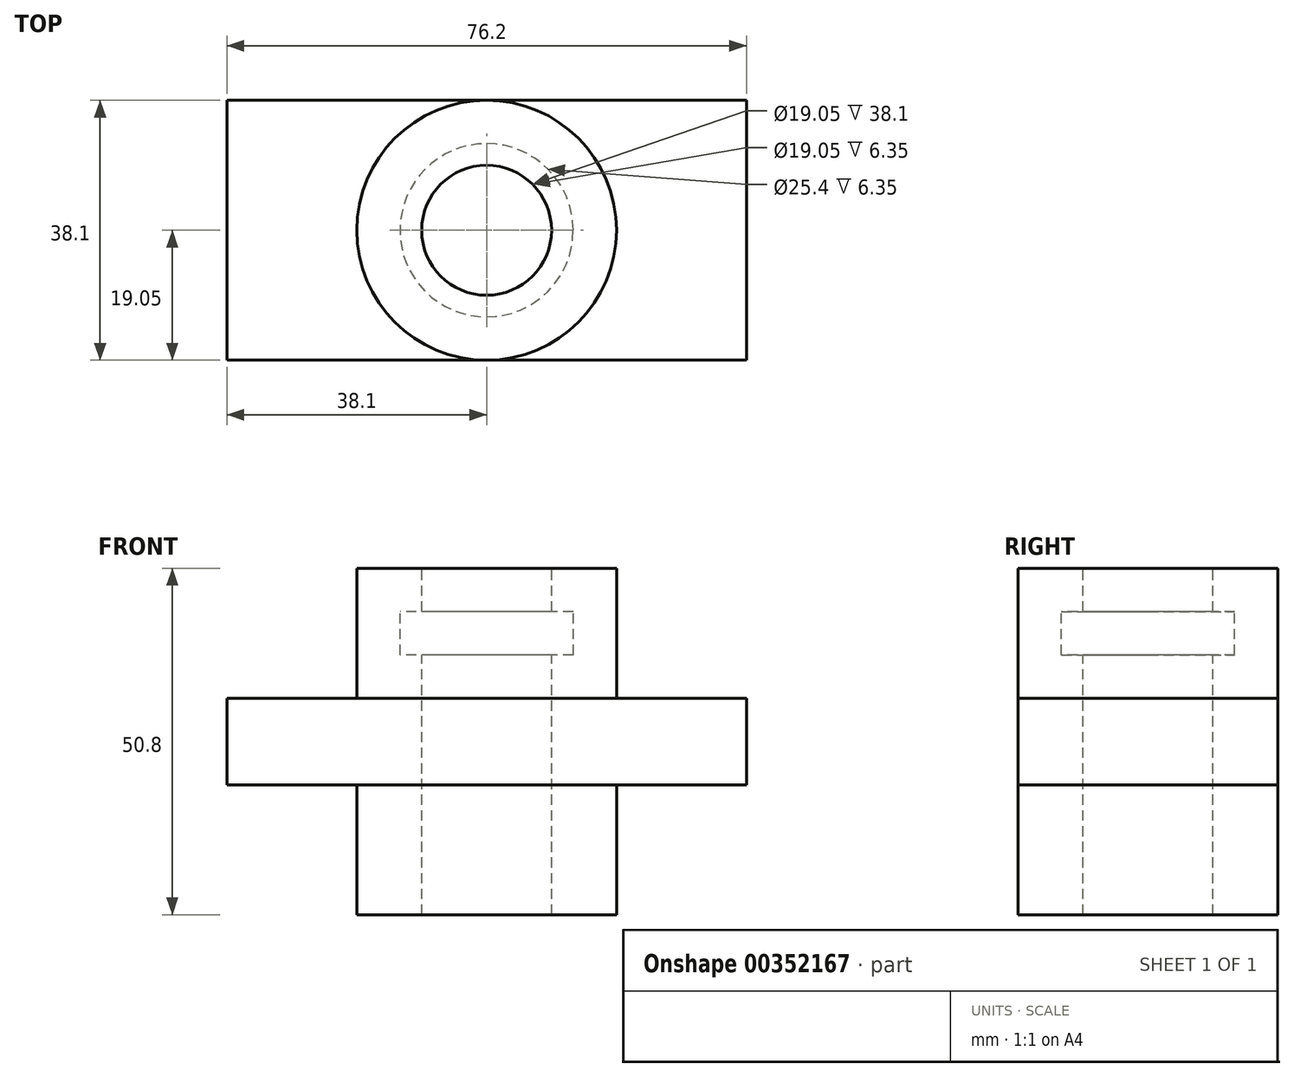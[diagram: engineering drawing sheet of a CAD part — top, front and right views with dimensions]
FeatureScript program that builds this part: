
annotation { "Feature Type Name" : "Feature", "Feature Type Description" : "" }
export const myFeature = defineFeature(function(context is Context, id is Id, definition is map)
    precondition{}
    {
        {
            var Q0;
            Q0=qCreatedBy(makeId("Top.planeOp"),FACE);
            var sketch = newSketch(context, id + "F0", { "sketchPlane" : qUnion([Q0])});
            skLineSegment(sketch, "E0.bottom", {"start": v(-38.1, -19.05) * mm, "end": v(38.1, -19.05) * mm});
            skLineSegment(sketch, "E0.top", {"start": v(-38.1, 19.05) * mm, "end": v(38.1, 19.05) * mm});
            skLineSegment(sketch, "E0.left", {"start": v(-38.1, -19.05) * mm, "end": v(-38.1, 19.05) * mm});
            skLineSegment(sketch, "E0.right", {"start": v(38.1, -19.05) * mm, "end": v(38.1, 19.05) * mm});
            skSolve(sketch);
        }
        {
            var Q0;
            Q0 = qSketchRegion(id + "F0", true);
            extrude(context, id + "F1", {"entities" : qUnion([Q0]), "endBound" : BoundingType.SYMMETRIC, "depth" : 12.7 * mm});
        }
        {
            var Q0;
            Q0=qCreatedBy(makeId("Top.planeOp"),FACE);
            var sketch = newSketch(context, id + "F2", { "sketchPlane" : qUnion([Q0])});
            skCircle(sketch, "E1", {"center": v(0, 0) * mm, "radius": 19.05 * mm});
            skSolve(sketch);
        }
        {
            var Q0;
            Q0 = qSketchRegion(id + "F2", true);
            extrude(context, id + "F3", {"entities" : qUnion([Q0]), "operationType" : NewBodyOperationType.ADD, "endBound" : BoundingType.SYMMETRIC, "depth" : 50.8 * mm});
        }
        {
            var Q0;
            Q0=qCreatedBy(makeId("Top.planeOp"),FACE);
            var sketch = newSketch(context, id + "F4", { "sketchPlane" : qUnion([Q0])});
            skCircle(sketch, "E2", {"center": v(0, 0) * mm, "radius": 9.53 * mm});
            skSolve(sketch);
        }
        {
            var Q0;
            Q0 = qSketchRegion(id + "F4", true);
            extrude(context, id + "F5", {"entities" : qUnion([Q0]), "operationType" : NewBodyOperationType.REMOVE, "endBound" : BoundingType.SYMMETRIC, "oppositeDirection" : true, "depth" : 50.8 * mm});
        }
        {
            var Q0;
            Q0=makeQuery(id+"F3.opExtrude","CAP_FACE",FACE,{"disambiguationData":[OSD([sQuery(id+"F2.wireOp",EDGE,"E1")])],"isStart":false});
            var sketch = newSketch(context, id + "F6", { "sketchPlane" : qUnion([Q0])});
            skPoint(sketch, "E3", {"position": v(0, 0) * mm});
            skCircle(sketch, "E4", {"center": v(0, 0) * mm, "radius": 12.7 * mm});
            skSolve(sketch);
        }
        {
            var Q0;
            Q0 = qSketchRegion(id + "F6", true);
            extrude(context, id + "F7", {"entities" : qUnion([Q0]), "operationType" : NewBodyOperationType.REMOVE, "oppositeDirection" : true, "depth" : 12.7 * mm, "hasSecondDirection" : true, "secondDirectionOppositeDirection" : true, "secondDirectionDepth" : 6.35 * mm});
        }
    });
